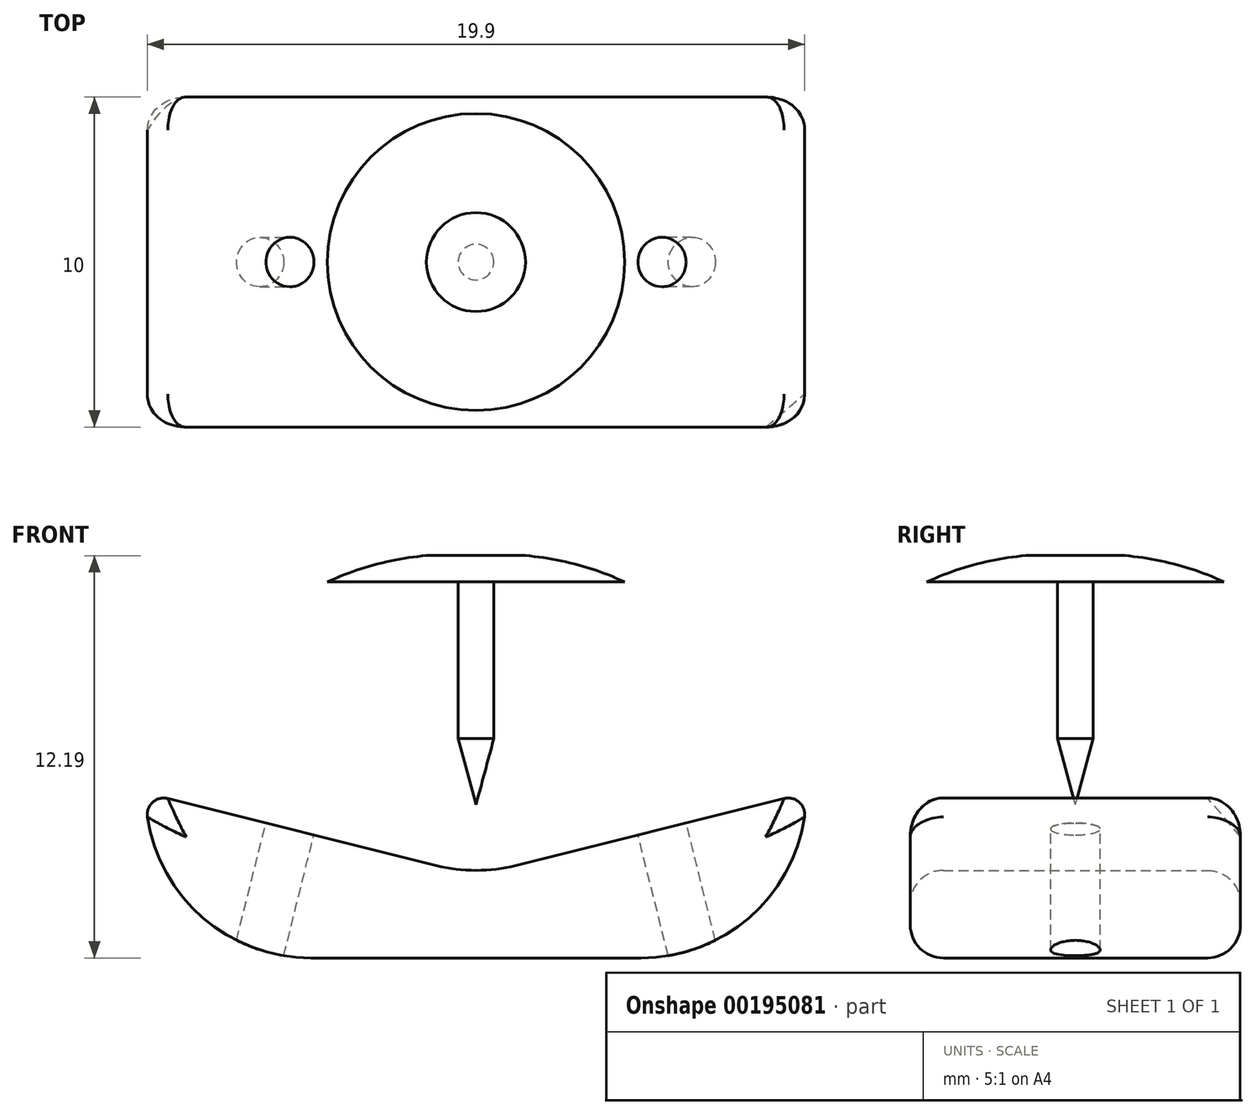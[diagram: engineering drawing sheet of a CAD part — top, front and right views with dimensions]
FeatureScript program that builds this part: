
annotation { "Feature Type Name" : "Feature", "Feature Type Description" : "" }
export const myFeature = defineFeature(function(context is Context, id is Id, definition is map)
    precondition{}
    {
        {
            var Q0;
            Q0=qCreatedBy(makeId("Front.planeOp"),FACE);
            var sketch = newSketch(context, id + "F0", { "sketchPlane" : qUnion([Q0])});
            skLineSegment(sketch, "E0.top", {"start": v(5, -2.5) * mm, "end": v(-5, -2.5) * mm});
            skLineSegment(sketch, "E0.left", {"start": v(10, 2.5) * mm, "end": v(10, 2.5) * mm});
            skLineSegment(sketch, "E0.right", {"start": v(-10, 2.5) * mm, "end": v(-10, 2.5) * mm});
            skPoint(sketch, "E0.middle", {"position": v(0, 0) * mm});
            skLineSegment(sketch, "E1", {"start": v(-10, 2.5) * mm, "end": v(-1.21, 0.3) * mm});
            skLineSegment(sketch, "E2", {"start": v(10, 2.5) * mm, "end": v(1.21, 0.3) * mm});
            skArc(sketch, "E3.filletArc", {"start": v(-1.21, 0.3) * mm, "mid": v(0, 0.15) * mm, "end": v(1.21, 0.3) * mm});
            skPoint(sketch, "E4.visualSharp", {"position": v(-10, -2.5) * mm});
            skArc(sketch, "E4.filletArc", {"start": v(-10, 2.5) * mm, "mid": v(-8.54, -1.04) * mm, "end": v(-5, -2.5) * mm});
            skPoint(sketch, "E5.visualSharp", {"position": v(10, -2.5) * mm});
            skArc(sketch, "E5.filletArc", {"start": v(5, -2.5) * mm, "mid": v(8.54, -1.04) * mm, "end": v(10, 2.5) * mm});
            skSolve(sketch);
        }
        {
            var Q0;
            Q0 = qSketchRegion(id + "F0", true);
            extrude(context, id + "F1", {"entities" : qUnion([Q0]), "endBound" : BoundingType.SYMMETRIC, "depth" : 10 * mm});
        }
        {
            var Q0;
            Q0=makeQuery(id+"F1.opExtrude","SWEPT_FACE",FACE,{"disambiguationData":[OSD([sQuery(id+"F0.wireOp",EDGE,"E2")])]});
            var sketch = newSketch(context, id + "F2", { "sketchPlane" : qUnion([Q0])});
            skCircle(sketch, "E6", {"center": v(5.8, 0) * mm, "radius": 4.5 * mm, "construction": true});
            skPoint(sketch, "E6.centerSnap0", {"position": v(1.25, 0) * mm});
            skCircle(sketch, "E7", {"center": v(5.8, 0) * mm, "radius": 0.75 * mm});
            skSolve(sketch);
        }
        {
            var Q0;
            Q0=makeQuery(id+"F2.imprint","IMPRINT",FACE,{"disambiguationData":[TD([[makeQuery(id+"F2.imprint","IMPRINT",EDGE,{"derivedFrom":sQuery(id+"F2.wireOp",EDGE,"E7")}),1.0]])]});
            var Q1;
            Q1=makeQuery(id+"F1.opExtrude","SWEPT_FACE",FACE,{"disambiguationData":[OSD([sQuery(id+"F0.wireOp",EDGE,"E5.filletArc")])]});
            extrude(context, id + "F3", {"entities" : qUnion([Q0]), "operationType" : NewBodyOperationType.REMOVE, "endBound" : BoundingType.UP_TO_SURFACE, "oppositeDirection" : true, "endBoundEntityFace" : qUnion([Q1]), "depth" : 25 * mm});
        }
        {
            var Q0;
            Q0=makeQuery(id+"F1.opExtrude","SWEPT_FACE",FACE,{"disambiguationData":[OSD([sQuery(id+"F0.wireOp",EDGE,"E1")])]});
            var sketch = newSketch(context, id + "F4", { "sketchPlane" : qUnion([Q0])});
            skCircle(sketch, "E8", {"center": v(-5.8, 0) * mm, "radius": 0.75 * mm});
            skPoint(sketch, "E8.centerSnap0", {"position": v(-10.3, 0) * mm});
            skCircle(sketch, "E9", {"center": v(-5.8, 0) * mm, "radius": 4.5 * mm, "construction": true});
            skSolve(sketch);
        }
        {
            var Q0;
            Q0 = qSketchRegion(id + "F4", true);
            var Q1;
            Q1=makeQuery(id+"F1.opExtrude","SWEPT_FACE",FACE,{"disambiguationData":[OSD([sQuery(id+"F0.wireOp",EDGE,"E4.filletArc")])]});
            extrude(context, id + "F5", {"entities" : qUnion([Q0]), "operationType" : NewBodyOperationType.REMOVE, "endBound" : BoundingType.UP_TO_SURFACE, "oppositeDirection" : true, "endBoundEntityFace" : qUnion([Q1]), "depth" : 25 * mm});
        }
        {
            var Q0;
            Q0=qCreatedBy(makeId("Front.planeOp"),FACE);
            var sketch = newSketch(context, id + "F6", { "sketchPlane" : qUnion([Q0])});
            skLineSegment(sketch, "E10.left", {"start": v(0, 8.9) * mm, "end": v(0, 2.14) * mm});
            skLineSegment(sketch, "E10.right", {"start": v(0.54, 8.9) * mm, "end": v(0.54, 4.14) * mm});
            skLineSegment(sketch, "E11", {"start": v(0, 2.14) * mm, "end": v(0.54, 4.14) * mm});
            skLineSegment(sketch, "E12.bottom", {"start": v(0.54, 8.9) * mm, "end": v(4.5, 8.9) * mm});
            skLineSegment(sketch, "E12.left", {"start": v(0, 8.9) * mm, "end": v(0, 9.7) * mm});
            skArc(sketch, "E13", {"start": v(4.5, 8.9) * mm, "mid": v(3.03, 9.43) * mm, "end": v(1.5, 9.7) * mm});
            skLineSegment(sketch, "E14", {"start": v(1.5, 9.7) * mm, "end": v(0, 9.7) * mm});
            skLineSegment(sketch, "E15", {"start": v(0, 9.7) * mm, "end": v(0, 9.7) * mm});
            skLineSegment(sketch, "E16", {"start": v(0, 12.69) * mm, "end": v(0, 0) * mm, "construction": true});
            skSolve(sketch);
        }
        {
            var Q0;
            Q0 = qSketchRegion(id + "F6", true);
            var Q1;
            Q1=sQuery(id+"F6.wireOp",EDGE,"E16");
            revolve(context, id + "F7", {"entities" : qUnion([Q0]), "axis" : qUnion([Q1]), "revolveType" : RevolveType.FULL});
        }
        {
            var Q0;
            Q0=makeQuery(id+"F1.opExtrude","CAP_FACE",FACE,{"disambiguationData":[OSD([sQuery(id+"F0.wireOp",EDGE,"E0.top"),sQuery(id+"F0.wireOp",EDGE,"E1"),sQuery(id+"F0.wireOp",EDGE,"E2"),sQuery(id+"F0.wireOp",EDGE,"E3.filletArc"),sQuery(id+"F0.wireOp",EDGE,"E4.filletArc"),sQuery(id+"F0.wireOp",EDGE,"E5.filletArc")])],"isStart":false});
            var Q1;
            Q1=makeQuery(id+"F1.opExtrude","CAP_FACE",FACE,{"disambiguationData":[OSD([sQuery(id+"F0.wireOp",EDGE,"E0.top"),sQuery(id+"F0.wireOp",EDGE,"E1"),sQuery(id+"F0.wireOp",EDGE,"E2"),sQuery(id+"F0.wireOp",EDGE,"E3.filletArc"),sQuery(id+"F0.wireOp",EDGE,"E4.filletArc"),sQuery(id+"F0.wireOp",EDGE,"E5.filletArc")])],"isStart":true});
            fillet(context, id + "F8", {"entities" : qUnion([Q0, Q1]), "radius" : 1 * mm, "tangentPropagation" : true, "allowEdgeOverflow" : false});
        }
        {
            var Q0;
            Q0=makeQuery(id+"F1.opExtrude","SWEPT_EDGE",EDGE,{"disambiguationData":[OSD([sQuery(id+"F0.wireOp",EDGE,"E2"),sQuery(id+"F0.wireOp",EDGE,"E5.filletArc")])]});
            var Q1;
            Q1=makeQuery(id+"F1.opExtrude","SWEPT_EDGE",EDGE,{"disambiguationData":[OSD([sQuery(id+"F0.wireOp",EDGE,"E1"),sQuery(id+"F0.wireOp",EDGE,"E4.filletArc")])]});
            fillet(context, id + "F9", {"entities" : qUnion([Q0, Q1]), "radius" : .5 * mm, "tangentPropagation" : true, "allowEdgeOverflow" : false});
        }
    });
